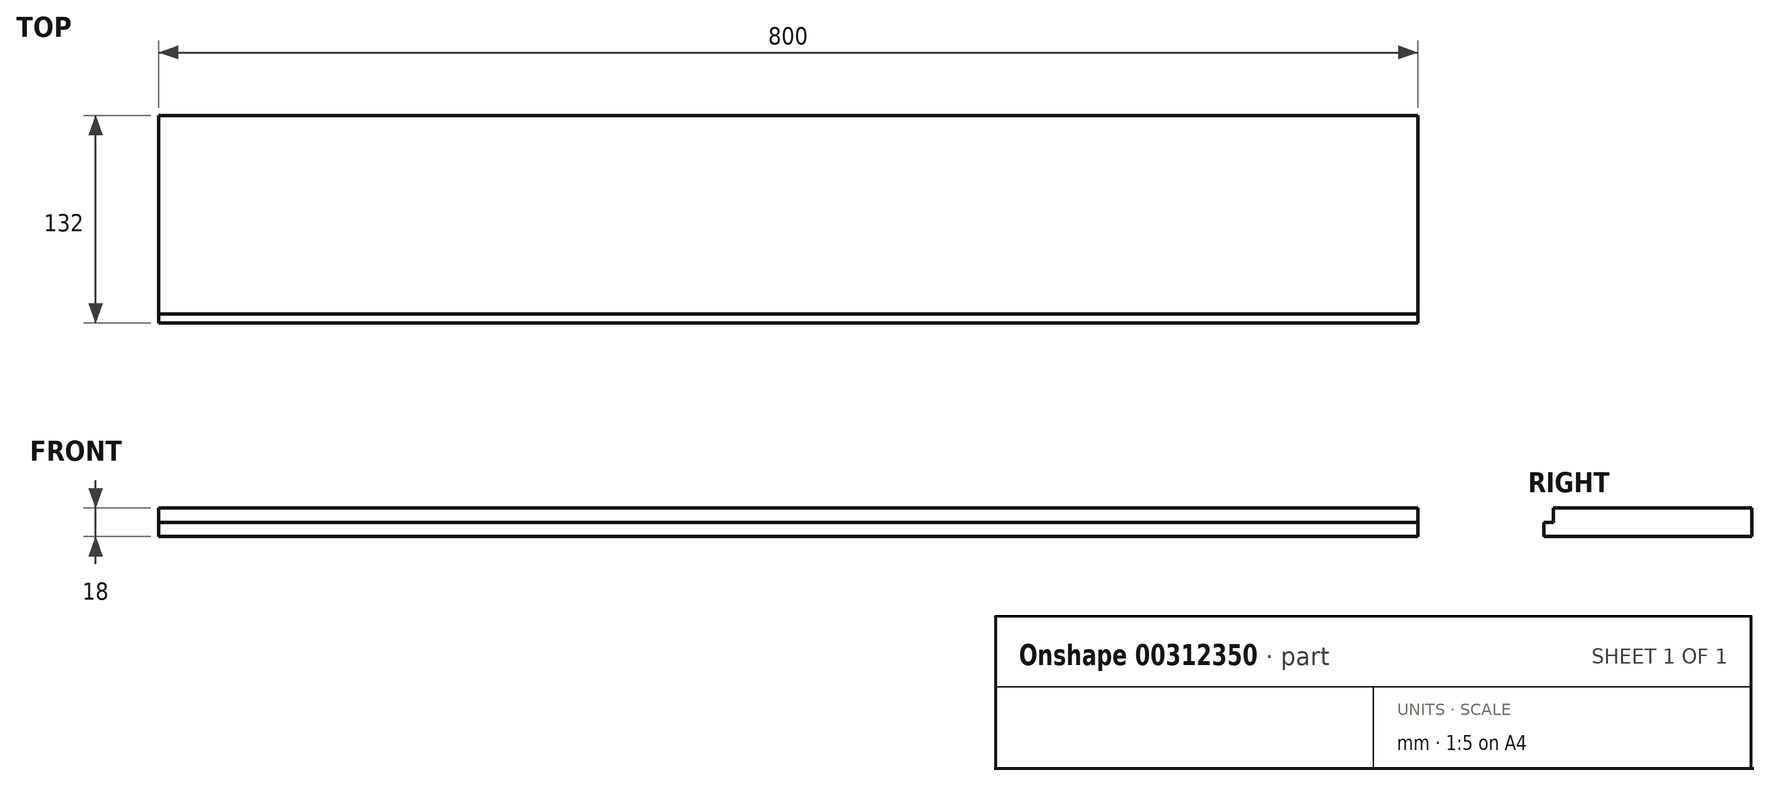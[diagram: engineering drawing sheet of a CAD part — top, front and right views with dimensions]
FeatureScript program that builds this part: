
annotation { "Feature Type Name" : "Feature", "Feature Type Description" : "" }
export const myFeature = defineFeature(function(context is Context, id is Id, definition is map)
    precondition{}
    {
        {
            var Q0;
            Q0=qCreatedBy(makeId("Top.planeOp"),FACE);
            var sketch = newSketch(context, id + "F0", { "sketchPlane" : qUnion([Q0])});
            skLineSegment(sketch, "E0", {"start": v(0, 0) * mm, "end": v(0, 132) * mm});
            skLineSegment(sketch, "E1", {"start": v(0, 132) * mm, "end": v(800, 132) * mm});
            skLineSegment(sketch, "E2", {"start": v(800, 132) * mm, "end": v(800, 0) * mm});
            skLineSegment(sketch, "E3", {"start": v(800, 0) * mm, "end": v(0, 0) * mm});
            skLineSegment(sketch, "E4", {"start": v(0, 0) * mm, "end": v(0, 6) * mm});
            skSolve(sketch);
        }
        {
            var Q0;
            {var subQ0=sQuery(id+"F0.wireOp",EDGE,"E1");Q0=makeQuery(id+"F0.imprint","IMPRINT",FACE,{"disambiguationData":[TD([[makeQuery(id+"F0.imprint","IMPRINT",EDGE,{"derivedFrom":subQ0}),-1.0]])]});}
            extrude(context, id + "F1", {"entities" : qUnion([Q0]), "depth" : 18 * mm, "offsetDistance" : 25 * mm});
        }
        {
            var Q0;
            Q0=makeQuery(id+"F1.opExtrude","SWEPT_FACE",FACE,{"disambiguationData":[OSD([sQuery(id+"F0.wireOp",EDGE,"E3")])]});
            var sketch = newSketch(context, id + "F2", { "sketchPlane" : qUnion([Q0])});
            skLineSegment(sketch, "E5", {"start": v(0, 0) * mm, "end": v(0, 9) * mm});
            skLineSegment(sketch, "E6", {"start": v(0, 9) * mm, "end": v(800, 9) * mm});
            skSolve(sketch);
        }
        {
            var Q0;
            {var subQ0=sQuery(id+"F2.wireOp",EDGE,"E6");Q0=makeQuery(id+"F2.imprint","IMPRINT",FACE,{"disambiguationData":[TD([[makeQuery(id+"F2.imprint","IMPRINT",EDGE,{"derivedFrom":subQ0}),1.0]])]});}
            extrude(context, id + "F3", {"entities" : qUnion([Q0]), "operationType" : NewBodyOperationType.REMOVE, "oppositeDirection" : true, "depth" : 6 * mm, "offsetDistance" : 25 * mm});
        }
    });
